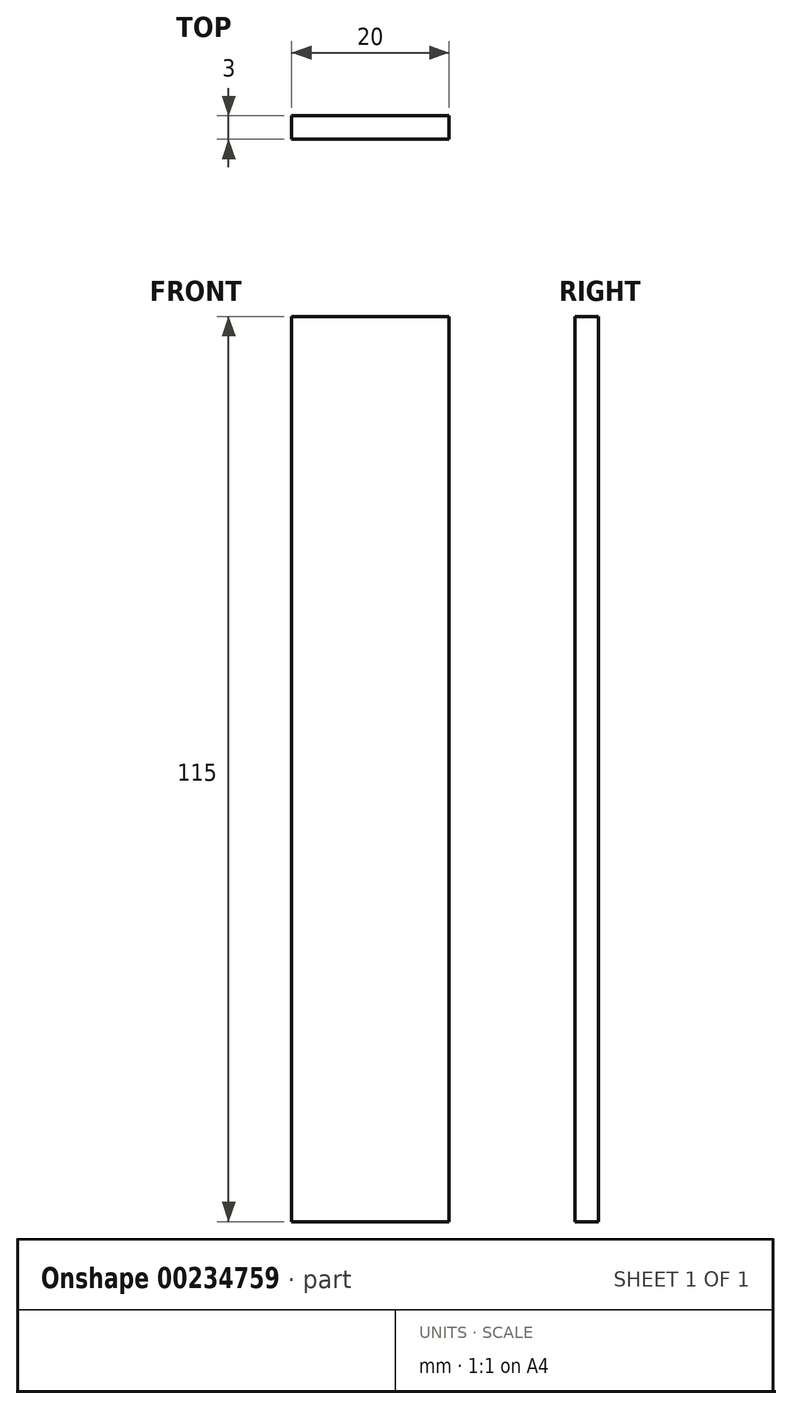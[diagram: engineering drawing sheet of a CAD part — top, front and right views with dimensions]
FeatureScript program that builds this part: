
annotation { "Feature Type Name" : "Feature", "Feature Type Description" : "" }
export const myFeature = defineFeature(function(context is Context, id is Id, definition is map)
    precondition{}
    {
        {
            var Q0;
            Q0=qCreatedBy(makeId("Front.planeOp"),FACE);
            var sketch = newSketch(context, id + "F0", { "sketchPlane" : qUnion([Q0])});
            skLineSegment(sketch, "E0.bottom", {"start": v(10, -57.5) * mm, "end": v(-10, -57.5) * mm});
            skLineSegment(sketch, "E0.top", {"start": v(10, 57.5) * mm, "end": v(-10, 57.5) * mm});
            skLineSegment(sketch, "E0.left", {"start": v(10, -57.5) * mm, "end": v(10, 57.5) * mm});
            skLineSegment(sketch, "E0.right", {"start": v(-10, -57.5) * mm, "end": v(-10, 57.5) * mm});
            skPoint(sketch, "E0.middle", {"position": v(0, 0) * mm});
            skSolve(sketch);
        }
        {
            var Q0;
            Q0 = qSketchRegion(id + "F0", true);
            extrude(context, id + "F1", {"entities" : qUnion([Q0]), "depth" : 3 * mm});
        }
    });
